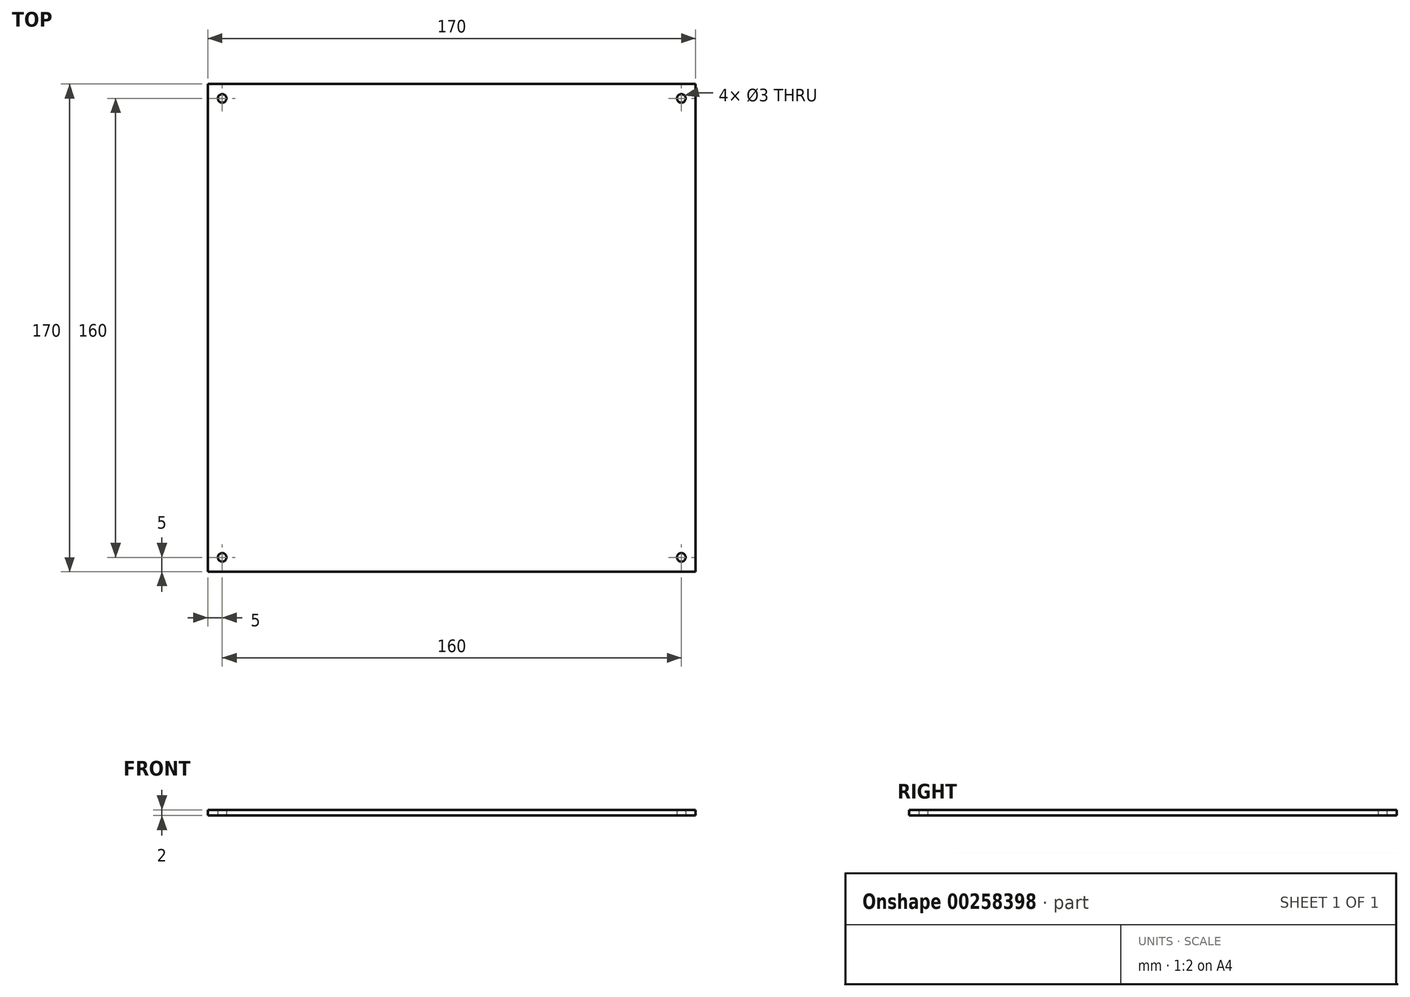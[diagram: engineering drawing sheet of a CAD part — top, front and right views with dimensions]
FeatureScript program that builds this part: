
annotation { "Feature Type Name" : "Feature", "Feature Type Description" : "" }
export const myFeature = defineFeature(function(context is Context, id is Id, definition is map)
    precondition{}
    {
        {
            var Q0;
            Q0=qCreatedBy(makeId("Top.planeOp"),FACE);
            var sketch = newSketch(context, id + "F0", { "sketchPlane" : qUnion([Q0])});
            skLineSegment(sketch, "E0.bottom", {"start": v(85, -85) * mm, "end": v(-85, -85) * mm});
            skLineSegment(sketch, "E0.top", {"start": v(85, 85) * mm, "end": v(-85, 85) * mm});
            skLineSegment(sketch, "E0.left", {"start": v(85, -85) * mm, "end": v(85, 85) * mm});
            skLineSegment(sketch, "E0.right", {"start": v(-85, -85) * mm, "end": v(-85, 85) * mm});
            skPoint(sketch, "E0.middle", {"position": v(0, 0) * mm});
            skCircle(sketch, "E1", {"center": v(-80, 80) * mm, "radius": 1.5 * mm});
            skCircle(sketch, "E2.MirrorC", {"center": v(80, 80) * mm, "radius": 1.5 * mm});
            skCircle(sketch, "E3.MirrorC", {"center": v(-80, -80) * mm, "radius": 1.5 * mm});
            skCircle(sketch, "E4.MirrorC", {"center": v(80, -80) * mm, "radius": 1.5 * mm});
            skSolve(sketch);
        }
        {
            var Q0;
            Q0=makeQuery(id+"F0.imprint","IMPRINT",FACE,{"disambiguationData":[TD([[makeQuery(id+"F0.imprint","IMPRINT",EDGE,{"derivedFrom":sQuery(id+"F0.wireOp",EDGE,"E0.bottom")}),-1.0]])]});
            extrude(context, id + "F1", {"entities" : qUnion([Q0]), "depth" : 2 * mm});
        }
    });
